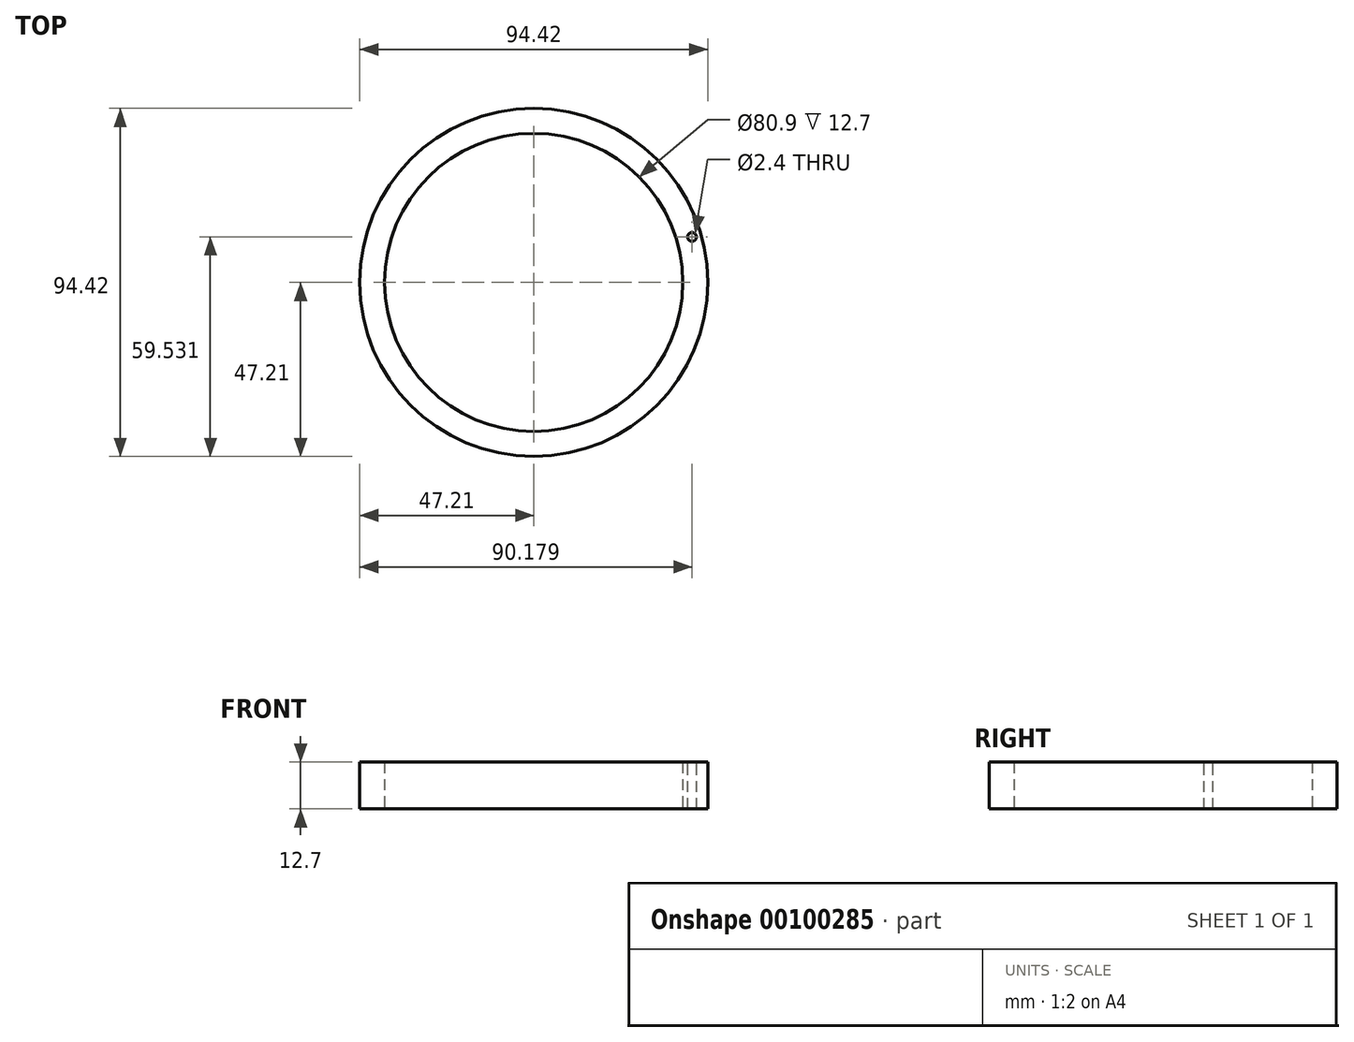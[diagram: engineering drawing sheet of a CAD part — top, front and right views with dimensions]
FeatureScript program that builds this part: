
annotation { "Feature Type Name" : "Feature", "Feature Type Description" : "" }
export const myFeature = defineFeature(function(context is Context, id is Id, definition is map)
    precondition{}
    {
        {
            var Q0;
            Q0=qCreatedBy(makeId("Top.planeOp"),FACE);
            var sketch = newSketch(context, id + "F0", { "sketchPlane" : qUnion([Q0])});
            skCircle(sketch, "E0", {"center": v(0, 0) * mm, "radius": 47.21 * mm});
            skCircle(sketch, "E1", {"center": v(0, 0) * mm, "radius": 40.45 * mm});
            skSolve(sketch);
        }
        {
            var Q0;
            Q0=makeQuery(id+"F0.imprint","IMPRINT",FACE,{"disambiguationData":[TD([[makeQuery(id+"F0.imprint","IMPRINT",EDGE,{"derivedFrom":sQuery(id+"F0.wireOp",EDGE,"E0")}),1.0]])]});
            extrude(context, id + "F1", {"entities" : qUnion([Q0]), "depth" : 25.4 * mm});
        }
        {
            var Q0;
            Q0=makeQuery(id+"F1.opExtrude","CAP_FACE",FACE,{"disambiguationData":[OSD([sQuery(id+"F0.wireOp",EDGE,"E0"),sQuery(id+"F0.wireOp",EDGE,"E1")])],"isStart":false});
            extrude(context, id + "F2", {"entities" : qUnion([Q0]), "operationType" : NewBodyOperationType.REMOVE, "oppositeDirection" : true, "depth" : 12.7 * mm});
        }
        {
            var Q0;
            Q0=makeQuery(id+"F2.boolean.opBoolean","COPY",FACE,{"derivedFrom":makeQuery(id+"F2.opExtrude","CAP_FACE",FACE,{"disambiguationData":[OSD([sQuery(id+"F0.wireOp",EDGE,"E0"),sQuery(id+"F0.wireOp",EDGE,"E1")])],"isStart":false})});
            var sketch = newSketch(context, id + "F3", { "sketchPlane" : qUnion([Q0])});
            skPoint(sketch, "E2", {"position": v(42.97, 12.32) * mm});
            skSolve(sketch);
        }
        {
            var Q0;
            Q0=sQuery(id+"F3.wireOp",VERTEX,"E2");
            var Q1;
            Q1=makeQuery(id+"F1.opExtrude","SWEPT_BODY",BODY,{"disambiguationData":[OSD([sQuery(id+"F0.wireOp",EDGE,"E0"),sQuery(id+"F0.wireOp",EDGE,"E1")])]});
            hole(context, id + "F4", {"style" : HoleStyle.SIMPLE, "endStyle" : HoleEndStyle.THROUGH, "standardTappedOrClearance" : lookupTablePath({ "standard" : "ISO", "engagement" : "75%", "pitch" : "0.6 mm", "size" : "M3", "type" : "Tapped" }), "standardBlindInLast" : lookupTablePath({ "standard" : "ISO", "engagement" : "75%", "pitch" : "0.6 mm", "size" : "M3", "type" : "Tapped" }), "holeDiameter" : 2.4 * mm, "locations" : qUnion([Q0]), "scope" : qUnion([Q1]), "isTappedThrough" : true, "showTappedDepth" : true});
        }
    });
